# Revit family: 0048751 Feilo Sylvania Lighting Fixture SYLPRF SUP LED G3 1500MM T 4K QC MW
name_source: partatom
category: Lighting Fixtures
revit_build: Autodesk Revit 2016 (Build: 20150220_1215(x64)
units: mm (PartAtom-declared; Revit-internal decimal feet)

## family parameters
Cut with Voids When Loaded = No
Host = Face
Light Source = Yes
OmniClass Number = 23.80.70.11.14
OmniClass Title = General Luminaries, Directional
Part Type = Normal
Room Calculation Point = No
Round Connector Dimension = Use Diameter
Shared = No

## types (1)
- 0048751 SYLPRF SUP LED G3 1500MM T 4K QC MW
    AccessoryMaterial = Diffuser-Sylvania-Glow
    Apparent Load = 47 VA
    Assembly Code = D5020200
    AssetType = Fixed
    BodyMaterial = Body-Sylvania-Gray
    ClassificationName = Uniclass2015
    ClassificationValue = EF_70_80
    Color Filter = 16777215
    Cost = 0 $
    Default Elevation = 1219 mm
    Description = Sylproof Superia, integrated LED weatherproof luminaire with quick connector, with UV stabilized flat diffuser and linear prisms designed to achieve uniform lit appearance, optimise light output and to reduce glare, stainless steel diffuser clips and fixing brackets for surface and wall mounting. L 1578 mm x W 110 mm x H 78 mm size, Polycarbonate housing, Polycarbonate diffuser, Non dimmable,   4000K, CRI80,  6800 lm, 47 W, 145 lm/W, nominal average life (h):50000, energy class: A++ A+ A Class I,IK08, IP65.
    DiffuserMaterial = Diffuser-Sylvania-Transparent
    Dimming Lamp Color Temperature Shift = <None>
    DimmingControlOptions = Non dimmable
    DocumentationLiterature = http://www.sylvania-lighting.com
    DurationUnit = hours
    ElectricShockClassification = Class I
    Emit Shape Visible in Rendering = No
    Emit from Rectangle Length = 1552 mm  [stored 5.09186 ft]
    Emit from Rectangle Width = 90 mm  [stored 0.295276 ft]
    ExpectedLife = 50000
    IfcExportAs = IfcLightFixtureType
    IfcExportType = IfcLightFixtureType
    ImpactProtectionIndex = IK08
    IngressProtection = IP65
    InputNominalFrequency = 50/60 Hz
    InputVoltage = 220-240V~
    Keynote = 16500
    Lamp = LED
    LampColourRenderingIndex = 80
    LampColourTemperature = 4000 K
    LampMacAdamStep = 3
    LampNominalLuminous = 6800 lm
    LampsType = LED
    Length = 1572 mm  [stored 5.15748 ft]
    LuminousEfficacy = 145 lm/W
    Manufacturer = Feilo Sylvania
    ManufacturerName = Feilo Sylvania
    Material = polycarbonate housing, polycarbonate diffuser
    Model = SYLPRF SUP LED G3 1500MM T 4K QC MW
    ModelNumber = 0048751
    ModelReference = SYLPRF SUP LED G3 1500MM T 4K QC MW
    Name = SYLPRF SUP LED G3 1500MM T 4K QC MW
    NominalHeight = 78 mm  [stored 0.255906 ft]
    NominalLength = 1578 mm  [stored 5.17717 ft]
    NominalWidth = 0 mm  [stored 0 ft]
    Photometric Web File = 0048751.ies
    PowerConsumption = 47 W
    PowerFactor = 0
    ReflectorMaterial = <By Category>
    Tilt Angle = -90.00°
    Type Image = <None>
    TypeName = SYLPRF SUP LED G3 1500MM T 4K QC MW
    URL = http://www.sylvania-lighting.com
    Voltage = 230 V
    Weight = 2.46 kg
    Width = 110 mm  [stored 0.360892 ft]

note: [stored X ft] marks values corroborated as IEEE doubles in the binary element streams (Revit-internal decimal feet)

## geometry (parser evidence)
native form markers: Sweep x5
no freeform markers — native parametric forms only
